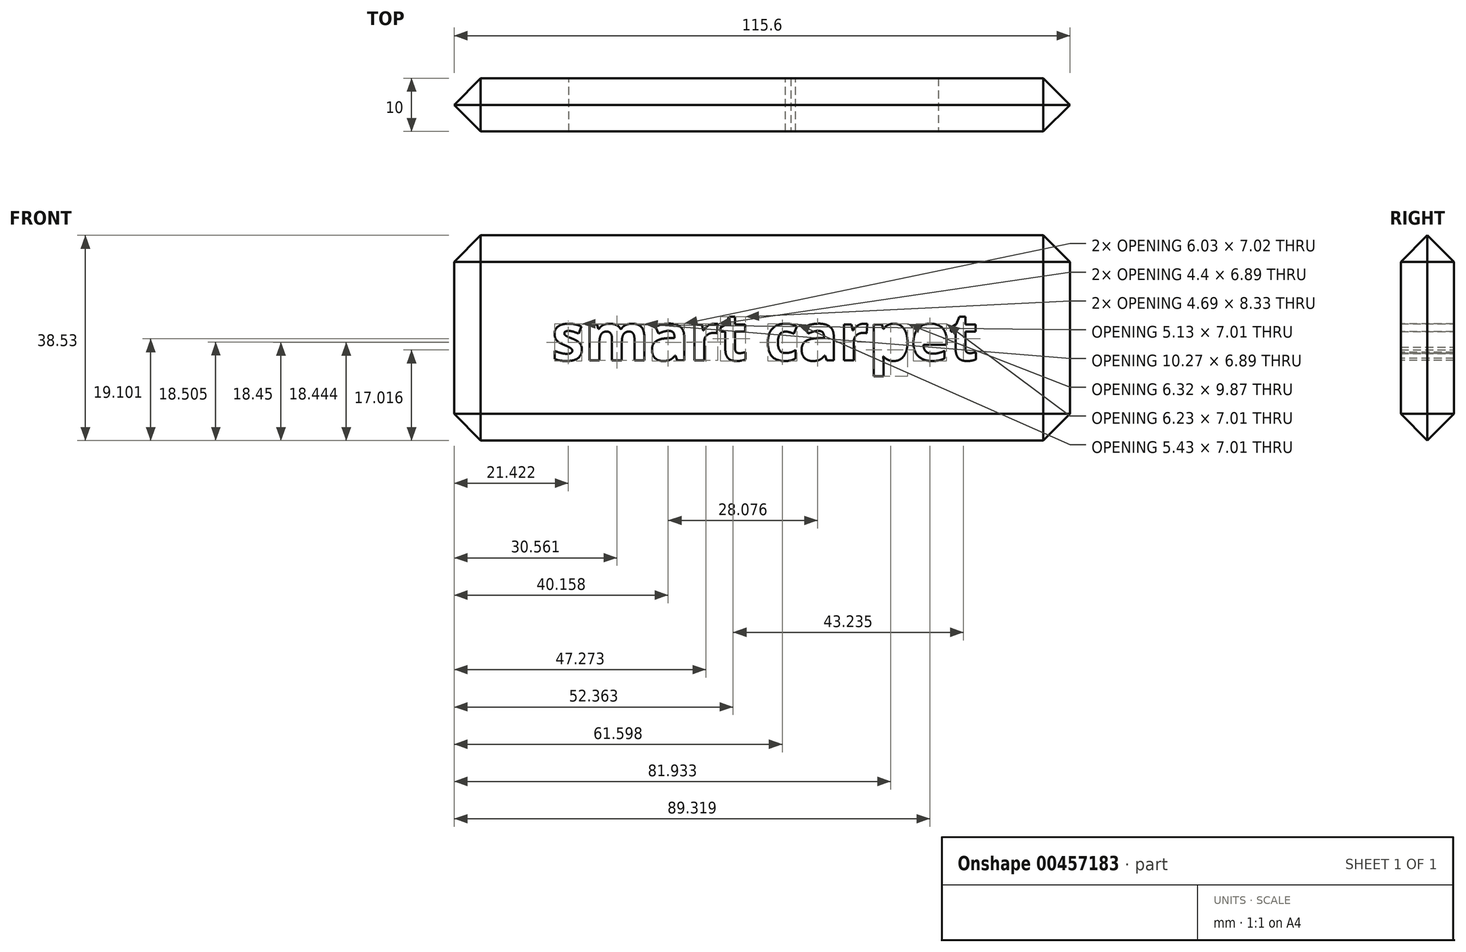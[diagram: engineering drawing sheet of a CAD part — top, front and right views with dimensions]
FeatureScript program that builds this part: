
annotation { "Feature Type Name" : "Feature", "Feature Type Description" : "" }
export const myFeature = defineFeature(function(context is Context, id is Id, definition is map)
    precondition{}
    {
        {
            var Q0;
            Q0=qCreatedBy(makeId("Front.planeOp"),FACE);
            var sketch = newSketch(context, id + "F0", { "sketchPlane" : qUnion([Q0])});
            skLineSegment(sketch, "E0.bottom", {"start": v(-57.8, 21.43) * mm, "end": v(57.8, 21.43) * mm});
            skLineSegment(sketch, "E0.top", {"start": v(-57.8, -17.1) * mm, "end": v(57.8, -17.1) * mm});
            skLineSegment(sketch, "E0.left", {"start": v(-57.8, 21.43) * mm, "end": v(-57.8, -17.1) * mm});
            skLineSegment(sketch, "E0.right", {"start": v(57.8, 21.43) * mm, "end": v(57.8, -17.1) * mm});
            skPoint(sketch, "E0.middle", {"position": v(0, 2.17) * mm});
            skText(sketch, "E1", { "text": "smart carpet", "fontName": "OpenSans-Bold.ttf"});
            const initialGuessF0  = {"E1": [-0.0395, -0.00204, 1, 0, 0.00892]};
            skSetInitialGuess(sketch, initialGuessF0);
            skSolve(sketch);
        }
        {
            var Q0;
            Q0=makeQuery(id+"F0.imprint","IMPRINT",FACE,{"disambiguationData":[TD([[makeQuery(id+"F0.imprint","IMPRINT",EDGE,{"derivedFrom":sQuery(id+"F0.wireOp",EDGE,"E0.bottom")}),-1.0]])]});
            extrude(context, id + "F1", {"entities" : qUnion([Q0]), "endBound" : BoundingType.SYMMETRIC, "depth" : 10 * mm});
        }
        {
            var Q0;
            Q0=makeQuery(id+"F1.opExtrude","SWEPT_FACE",FACE,{"disambiguationData":[OSD([sQuery(id+"F0.wireOp",EDGE,"E0.right")])]});
            var Q1;
            Q1=makeQuery(id+"F1.opExtrude","SWEPT_FACE",FACE,{"disambiguationData":[OSD([sQuery(id+"F0.wireOp",EDGE,"E0.top")])]});
            var Q2;
            Q2=makeQuery(id+"F1.opExtrude","SWEPT_FACE",FACE,{"disambiguationData":[OSD([sQuery(id+"F0.wireOp",EDGE,"E0.bottom")])]});
            var Q3;
            Q3=makeQuery(id+"F1.opExtrude","SWEPT_FACE",FACE,{"disambiguationData":[OSD([sQuery(id+"F0.wireOp",EDGE,"E0.left")])]});
            chamfer(context, id + "F2", {"entities" : qUnion([Q0, Q1, Q2, Q3]), "width" : 5 * mm, "tangentPropagation" : true});
        }
    });
